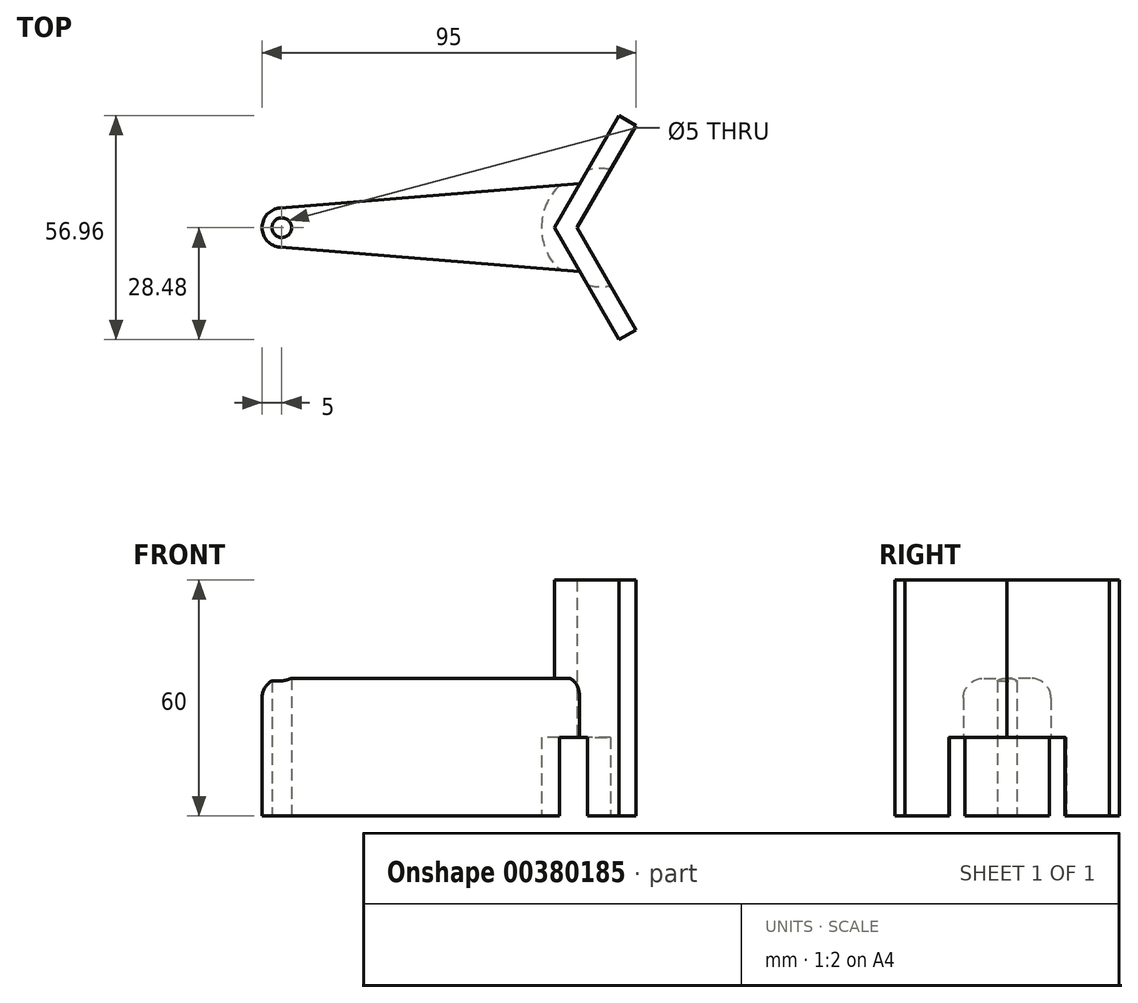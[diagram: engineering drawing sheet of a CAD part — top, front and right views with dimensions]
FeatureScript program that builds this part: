
annotation { "Feature Type Name" : "Feature", "Feature Type Description" : "" }
export const myFeature = defineFeature(function(context is Context, id is Id, definition is map)
    precondition{}
    {
        {
            var Q0;
            Q0=qCreatedBy(makeId("Top.planeOp"),FACE);
            var sketch = newSketch(context, id + "F0", { "sketchPlane" : qUnion([Q0])});
            skArc(sketch, "E0", {"start": v(-75.4, 4.98) * mm, "mid": v(-80, 0) * mm, "end": v(-75.4, -4.98) * mm});
            skLineSegment(sketch, "E1", {"start": v(0, 0) * mm, "end": v(15, 25.98) * mm});
            skLineSegment(sketch, "E2.MirrorCS", {"start": v(0, 0) * mm, "end": v(15, -25.98) * mm});
            skLineSegment(sketch, "E3", {"start": v(15, 25.98) * mm, "end": v(10.67, 28.48) * mm});
            skLineSegment(sketch, "E4", {"start": v(10.67, 28.48) * mm, "end": v(0.67, 11.16) * mm});
            skLineSegment(sketch, "E5", {"start": v(0.67, 11.16) * mm, "end": v(-75.4, 4.98) * mm});
            skLineSegment(sketch, "E6.MirrorCS", {"start": v(15, -25.98) * mm, "end": v(10.67, -28.48) * mm});
            skLineSegment(sketch, "E7.MirrorCS", {"start": v(10.67, -28.48) * mm, "end": v(0.67, -11.16) * mm});
            skLineSegment(sketch, "E8.MirrorCS", {"start": v(0.67, -11.16) * mm, "end": v(-75.4, -4.98) * mm});
            skCircle(sketch, "E9", {"center": v(-75, 0) * mm, "radius": 2.5 * mm});
            skSolve(sketch);
        }
        {
            var Q0;
            Q0=makeQuery(id+"F0.imprint","IMPRINT",FACE,{"disambiguationData":[TD([[makeQuery(id+"F0.imprint","IMPRINT",EDGE,{"derivedFrom":sQuery(id+"F0.wireOp",EDGE,"E0")}),1.0]])]});
            extrude(context, id + "F1", {"entities" : qUnion([Q0]), "depth" : 35 * mm});
        }
        {
            var Q0;
            Q0=makeQuery(id+"F1.opExtrude","CAP_FACE",FACE,{"disambiguationData":[OSD([sQuery(id+"F0.wireOp",EDGE,"E0"),sQuery(id+"F0.wireOp",EDGE,"E1"),sQuery(id+"F0.wireOp",EDGE,"E2.MirrorCS"),sQuery(id+"F0.wireOp",EDGE,"E3"),sQuery(id+"F0.wireOp",EDGE,"E4"),sQuery(id+"F0.wireOp",EDGE,"E5"),sQuery(id+"F0.wireOp",EDGE,"E6.MirrorCS"),sQuery(id+"F0.wireOp",EDGE,"E7.MirrorCS"),sQuery(id+"F0.wireOp",EDGE,"E8.MirrorCS"),sQuery(id+"F0.wireOp",EDGE,"E9")])],"isStart":false});
            var sketch = newSketch(context, id + "F2", { "sketchPlane" : qUnion([Q0])});
            skLineSegment(sketch, "E10.0", {"start": v(0, 0) * mm, "end": v(15, 25.98) * mm});
            skLineSegment(sketch, "E10.1", {"start": v(0, 0) * mm, "end": v(15, -25.98) * mm});
            skLineSegment(sketch, "E10.2", {"start": v(15, -25.98) * mm, "end": v(10.67, -28.48) * mm});
            skLineSegment(sketch, "E10.3", {"start": v(15, 25.98) * mm, "end": v(10.67, 28.48) * mm});
            skLineSegment(sketch, "E11", {"start": v(10.67, 28.48) * mm, "end": v(-5.77, 0) * mm});
            skLineSegment(sketch, "E12.MirrorCS", {"start": v(10.67, -28.48) * mm, "end": v(-5.77, 0) * mm});
            skSolve(sketch);
        }
        {
            var Q0;
            Q0=makeQuery(id+"F2.imprint","IMPRINT",FACE,{"disambiguationData":[TD([[makeQuery(id+"F2.imprint","IMPRINT",EDGE,{"derivedFrom":sQuery(id+"F2.wireOp",EDGE,"E10.0")}),1.0]])]});
            extrude(context, id + "F3", {"entities" : qUnion([Q0]), "operationType" : NewBodyOperationType.ADD, "depth" : 25 * mm});
        }
        {
            var Q0;
            Q0=makeQuery(id+"F1.opExtrude","CAP_EDGE",EDGE,{"disambiguationData":[OSD([sQuery(id+"F0.wireOp",EDGE,"E8.MirrorCS")])],"isStart":false});
            fillet(context, id + "F4", {"entities" : qUnion([Q0]), "radius" : 5 * mm, "tangentPropagation" : true, "allowEdgeOverflow" : false});
        }
        {
            var Q0;
            Q0=qCreatedBy(makeId("Top.planeOp"),FACE);
            var sketch = newSketch(context, id + "F5", { "sketchPlane" : qUnion([Q0])});
            skCircle(sketch, "E13", {"center": v(6, 0) * mm, "radius": 15 * mm});
            skSolve(sketch);
        }
        {
            var Q0;
            Q0=makeQuery(id+"F5.imprint","IMPRINT",FACE,{"disambiguationData":[TD([[makeQuery(id+"F5.imprint","IMPRINT",EDGE,{"derivedFrom":sQuery(id+"F5.wireOp",EDGE,"E13")}),1.0]])]});
            var Q1;
            Q1=sQuery(id+"F5.wireOp",EDGE,"E13");
            extrude(context, id + "F6", {"entities" : qUnion([Q0]), "operationType" : NewBodyOperationType.REMOVE, "surfaceEntities" : qUnion([Q1]), "depth" : 20 * mm});
        }
    });
